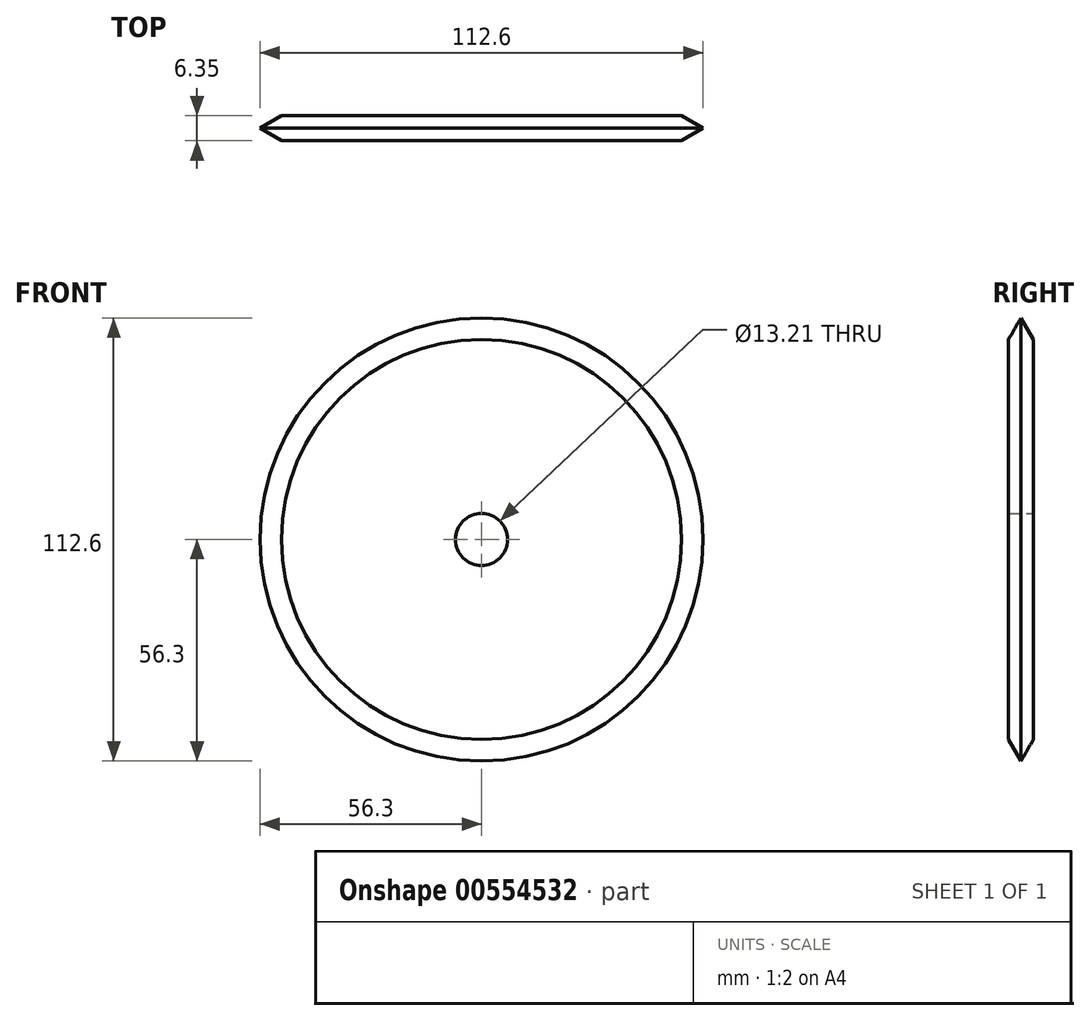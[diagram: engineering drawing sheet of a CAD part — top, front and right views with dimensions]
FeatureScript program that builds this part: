
annotation { "Feature Type Name" : "Feature", "Feature Type Description" : "" }
export const myFeature = defineFeature(function(context is Context, id is Id, definition is map)
    precondition{}
    {
        {
            var Q0;
            Q0=qCreatedBy(makeId("Front.planeOp"),FACE);
            var sketch = newSketch(context, id + "F0", { "sketchPlane" : qUnion([Q0])});
            skCircle(sketch, "E0", {"center": v(0, 0) * mm, "radius": 50.8 * mm});
            skSolve(sketch);
        }
        {
            var Q0;
            Q0=makeQuery(id+"F0.imprint","IMPRINT",FACE,{"disambiguationData":[TD([[makeQuery(id+"F0.imprint","IMPRINT",EDGE,{"derivedFrom":sQuery(id+"F0.wireOp",EDGE,"E0")}),1.0]])]});
            var Q1;
            Q1=sQuery(id+"F0.wireOp",EDGE,"E0");
            extrude(context, id + "F1", {"entities" : qUnion([Q0]), "surfaceEntities" : qUnion([Q1]), "depth" : 6.35 * mm, "offsetDistance" : 25.4 * mm});
        }
        {
            var Q0;
            Q0=sQuery(id+"F0.wireOp",VERTEX,"E0.center");
            var Q1;
            Q1=makeQuery(id+"F1.opExtrude","SWEPT_BODY",BODY,{"disambiguationData":[OSD([sQuery(id+"F0.wireOp",EDGE,"E0")])]});
            hole(context, id + "F2", {"style" : HoleStyle.SIMPLE, "endStyle" : HoleEndStyle.THROUGH, "oppositeDirection" : true, "holeDiameter" : 13.2 * mm, "isTappedThrough" : true, "tappedDepth" : 12.7 * mm, "tapClearance" : 3, "locations" : qUnion([Q0]), "scope" : qUnion([Q1])});
        }
        {
            var Q0;
            Q0=qCreatedBy(makeId("Top.planeOp"),FACE);
            var sketch = newSketch(context, id + "F3", { "sketchPlane" : qUnion([Q0])});
            skLineSegment(sketch, "E1", {"start": v(50.8, -6.35) * mm, "end": v(56.3, -3.17) * mm});
            skLineSegment(sketch, "E2", {"start": v(56.3, -3.18) * mm, "end": v(50.8, 0) * mm});
            skLineSegment(sketch, "E3", {"start": v(50.8, -6.35) * mm, "end": v(50.8, 0) * mm});
            skSolve(sketch);
        }
        {
            var Q0;
            Q0 = qSketchRegion(id + "F3", true);
            var Q1;
            Q1=makeQuery(id+"F1.opExtrude","CAP_EDGE",EDGE,{"disambiguationData":[OSD([sQuery(id+"F0.wireOp",EDGE,"E0")])],"isStart":false});
            revolve(context, id + "F4", {"operationType" : NewBodyOperationType.ADD, "entities" : qUnion([Q0]), "axis" : qUnion([Q1]), "revolveType" : RevolveType.FULL});
        }
    });
